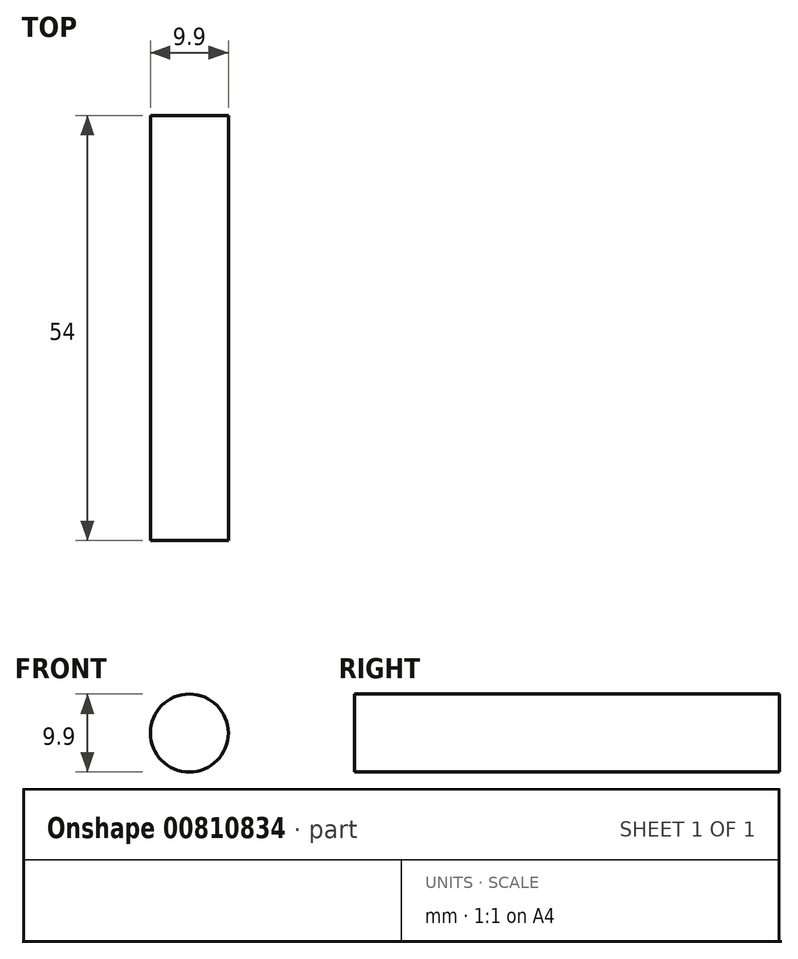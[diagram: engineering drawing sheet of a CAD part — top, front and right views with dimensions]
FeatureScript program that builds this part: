
annotation { "Feature Type Name" : "Feature", "Feature Type Description" : "" }
export const myFeature = defineFeature(function(context is Context, id is Id, definition is map)
    precondition{}
    {
        {
            var Q0;
            Q0=qCreatedBy(makeId("Front.planeOp"),FACE);
            var sketch = newSketch(context, id + "F0", { "sketchPlane" : qUnion([Q0])});
            skCircle(sketch, "E0", {"center": v(0, 0) * mm, "radius": 4.95 * mm});
            skSolve(sketch);
        }
        {
            var Q0;
            Q0=makeQuery(id+"F0.imprint","IMPRINT",FACE,{"disambiguationData":[TD([[makeQuery(id+"F0.imprint","IMPRINT",EDGE,{"derivedFrom":sQuery(id+"F0.wireOp",EDGE,"E0")}),1.0]])]});
            extrude(context, id + "F1", {"entities" : qUnion([Q0]), "depth" : 54 * mm, "offsetDistance" : 25 * mm});
        }
    });
